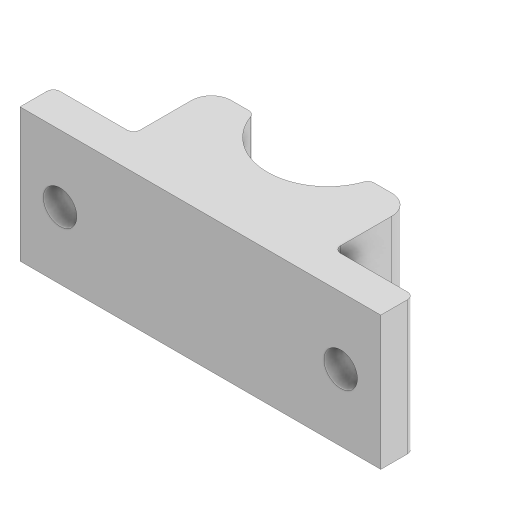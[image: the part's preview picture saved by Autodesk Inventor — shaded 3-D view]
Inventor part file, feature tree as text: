
AUTODESK INVENTOR PART (.ipt)
format: ipt  version: 2023 (Build 270158000, 158)  size: 142,336 bytes
history: native  units: mm
features: fillet x4, sketch x3, extrude x2, mirror x1
ambient origin geometry x8: Origin, YZ Plane, XZ Plane, XY Plane, X Axis, Y Axis, Z Axis, Center Point
bodies: Solid1 (feature_tree)
feature tree (10):
  extrude  "Extrusion1"  Depth=19.05mm
  extrude  "Extrusion2"  Depth=10.0mm
  mirror  "Mirror1"
  fillet  "Fillet2"  Radius=27.0mm
  fillet  "Fillet3"  Radius=20.0mm
  sketch  "Sketch3"  dims[d12=5.0mm d13=5.0mm d14=0.0mm d15=0.0mm d17=1.0mm d18=1.0mm d19=1.0mm d20=3.0mm]
  fillet  "Fillet4"  Radius=6.0mm
  fillet  "Fillet5"  Radius=10.0mm
  sketch  "Sketch1"  dims[d0=18.0mm d1=19.05mm]
  sketch  "Sketch2"  dims[d5=15.0mm d6=15.0mm d7=27.0mm d8=20.0mm d9=0.0mm d10=6.0mm d11=10.0mm]
